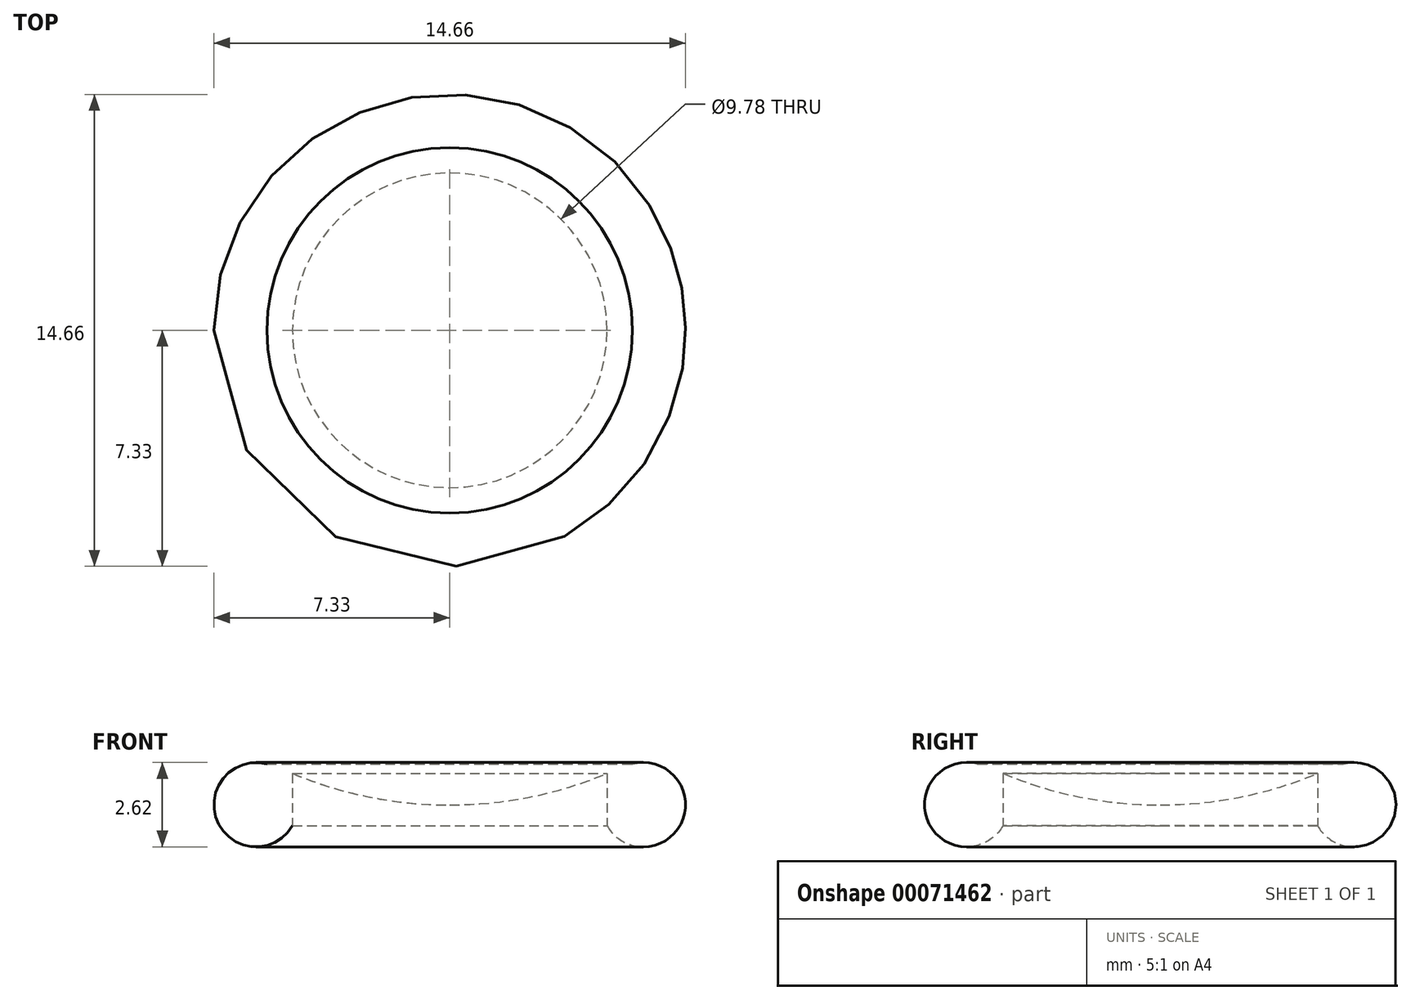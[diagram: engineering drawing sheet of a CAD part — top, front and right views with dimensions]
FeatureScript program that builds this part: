
annotation { "Feature Type Name" : "Feature", "Feature Type Description" : "" }
export const myFeature = defineFeature(function(context is Context, id is Id, definition is map)
    precondition{}
    {
        {
            var Q0;
            Q0=qCreatedBy(makeId("Front.planeOp"),FACE);
            var sketch = newSketch(context, id + "F0", { "sketchPlane" : qUnion([Q0])});
            skCircle(sketch, "E0", {"center": v(0, 0) * mm, "radius": 12.7 * mm});
            skLineSegment(sketch, "E1", {"start": v(0, 0) * mm, "end": v(0, 12.7) * mm});
            skLineSegment(sketch, "E2", {"start": v(0, 12.7) * mm, "end": v(0, -12.7) * mm});
            skLineSegment(sketch, "E3.bottom", {"start": v(0, -13.95) * mm, "end": v(-6.02, -13.95) * mm});
            skLineSegment(sketch, "E3.top", {"start": v(0, -11.43) * mm, "end": v(-6.02, -11.43) * mm});
            skLineSegment(sketch, "E3.left", {"start": v(0, -13.95) * mm, "end": v(0, -11.43) * mm});
            skLineSegment(sketch, "E3.right", {"start": v(-6.02, -13.95) * mm, "end": v(-6.02, -11.43) * mm});
            skCircle(sketch, "E4", {"center": v(-6.02, -12.7) * mm, "radius": 1.3 * mm});
            skLineSegment(sketch, "E5.bottom", {"start": v(0, -13.95) * mm, "end": v(-4.89, -13.95) * mm});
            skLineSegment(sketch, "E5.top", {"start": v(0, 1.29) * mm, "end": v(-4.89, 1.29) * mm});
            skLineSegment(sketch, "E5.left", {"start": v(0, -13.95) * mm, "end": v(0, 1.29) * mm});
            skLineSegment(sketch, "E5.right", {"start": v(-4.89, -13.95) * mm, "end": v(-4.89, 1.29) * mm});
            skSolve(sketch);
        }
        {
            var Q0;
            {var subQ6=sQuery(id+"F0.wireOp",EDGE,"E2");Q0=makeQuery(id+"F0.imprint","IMPRINT",FACE,{"disambiguationData":[TD([[makeQuery(id+"F0.imprint","IMPRINT",EDGE,{"derivedFrom":subQ6}),-1.0]])]});}
            var Q1;
            {var subQ0=sQuery(id+"F0.wireOp",EDGE,"E3.right");Q1=makeQuery(id+"F0.imprint","IMPRINT",FACE,{"disambiguationData":[TD([[makeQuery(id+"F0.imprint","IMPRINT",EDGE,{"derivedFrom":subQ0}),1.0]])]});}
            var Q2;
            {var subQ5=sQuery(id+"F0.wireOp",EDGE,"E3.right");Q2=makeQuery(id+"F0.imprint","IMPRINT",FACE,{"disambiguationData":[TD([[makeQuery(id+"F0.imprint","IMPRINT",EDGE,{"derivedFrom":subQ5}),-1.0]])]});}
            var Q3;
            {var subQ0=sQuery(id+"F0.wireOp",EDGE,"E3.top");var subQ1=sQuery(id+"F0.wireOp",EDGE,"E0");var subQ2=makeQuery(id+"F0.imprint","INTERSECT",VERTEX,{"derivedFrom":[subQ1,subQ0]});Q3=makeQuery(id+"F0.imprint","IMPRINT",FACE,{"disambiguationData":[TD([[makeQuery(id+"F0.imprint","IMPRINT",EDGE,{"disambiguationData":[TD([[subQ2,-1.0]])],"derivedFrom":subQ1}),1.0]])]});}
            var Q4;
            {var subQ0=sQuery(id+"F0.wireOp",EDGE,"E3.top");var subQ1=sQuery(id+"F0.wireOp",EDGE,"E0");var subQ2=makeQuery(id+"F0.imprint","INTERSECT",VERTEX,{"derivedFrom":[subQ1,subQ0]});Q4=makeQuery(id+"F0.imprint","IMPRINT",FACE,{"disambiguationData":[TD([[makeQuery(id+"F0.imprint","IMPRINT",EDGE,{"disambiguationData":[TD([[subQ2,-1.0]])],"derivedFrom":subQ1}),-1.0]])]});}
            var Q5;
            Q5=sQuery(id+"F0.wireOp",EDGE,"E5.left");
            revolve(context, id + "F1", {"entities" : qUnion([Q0, Q1, Q2, Q3, Q4]), "axis" : qUnion([Q5]), "revolveType" : RevolveType.FULL});
        }
    });
